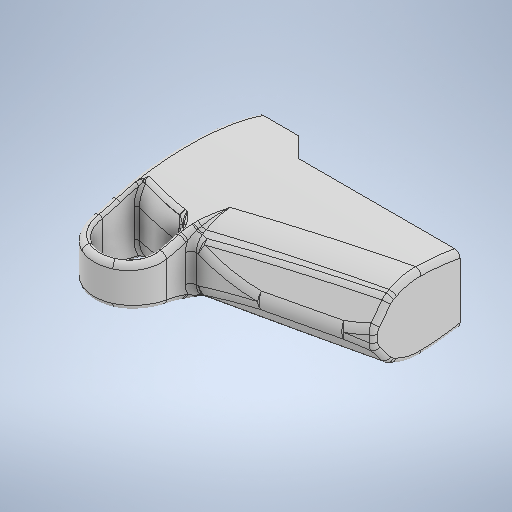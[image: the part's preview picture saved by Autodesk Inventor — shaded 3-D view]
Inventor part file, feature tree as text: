
AUTODESK INVENTOR PART (.ipt)
format: ipt  version: 2025 (Build 290162000, 162)  size: 1,472,512 bytes
history: native  units: in
note: dims shown in document units (in); Inventor stores cm internally (conversion verified against a paired STEP export)
features: fillet x12, extrude x7, other x6, sketch x5, chamfer x5, projected_geometry x3, mirror x1
ambient origin geometry x8: Origin, YZ Plane, XZ Plane, XY Plane, X Axis, Y Axis, Z Axis, Center Point
bodies: Body1 (feature_tree)
feature tree (39):
  other  "ソリッド1"
  sketch  "スケッチ1"
  extrude  "押し出し1"  Depth=3.3465in
  sketch  "スケッチ4"
  extrude  "押し出し4"  Depth=0.2756in
  extrude  "押し出し5"  Depth=9.8425in
  extrude  "押し出し6"  Depth=0.8661in TaperAngle=0.0deg
  extrude  "押し出し7"  Depth=0.8268in
  chamfer  "面取り1"  Distance=0.1181in
  chamfer  "面取り2"  Distance=0.1181in
  chamfer  "面取り3"  Distance=1.8504in
  chamfer  "面取り4"  Distance=1.1024in
  other  "作業平面3"
  other  "作業平面5"
  extrude  "押し出し8"  Depth=1.5354in
  other  "作業平面6"
  mirror  "ミラー1"
  chamfer  "面取り5"  Distance=3.3465in
  extrude  "押し出し9"  Depth=3.3465in TaperAngle=0.0deg
  fillet  "フィレット27"  Radius=3.3465in
  fillet  "フィレット28"  Radius=3.3465in
  fillet  "フィレット29"  Radius=0.1181in
  fillet  "フィレット30"  Radius=0.1181in
  fillet  "フィレット32"  Radius=0.1181in
  fillet  "フィレット35"  Radius=0.1181in
  fillet  "フィレット36"  Radius=0.3937in
  fillet  "フィレット37"  Radius=0.1575in
  fillet  "フィレット38"  Radius=0.5906in
  fillet  "フィレット42"  [1 undecoded]
  fillet  "フィレット43"  Radius=0.3937in
  fillet  "フィレット44"  Radius=1.9685in
  projected_geometry  "投影ループ2"
  sketch  "スケッチ5"
  projected_geometry  "投影ループ3"
  sketch  "スケッチ6"
  projected_geometry  "投影ループ4"
  other  "作業平面2"
  other  "作業平面4"
  sketch  "スケッチ7"
note: 1 required parameter value undecoded (feature->parameter linkage not recoverable at this tier; creation-order binding heuristic only, values carry confidence <= 0.55)
